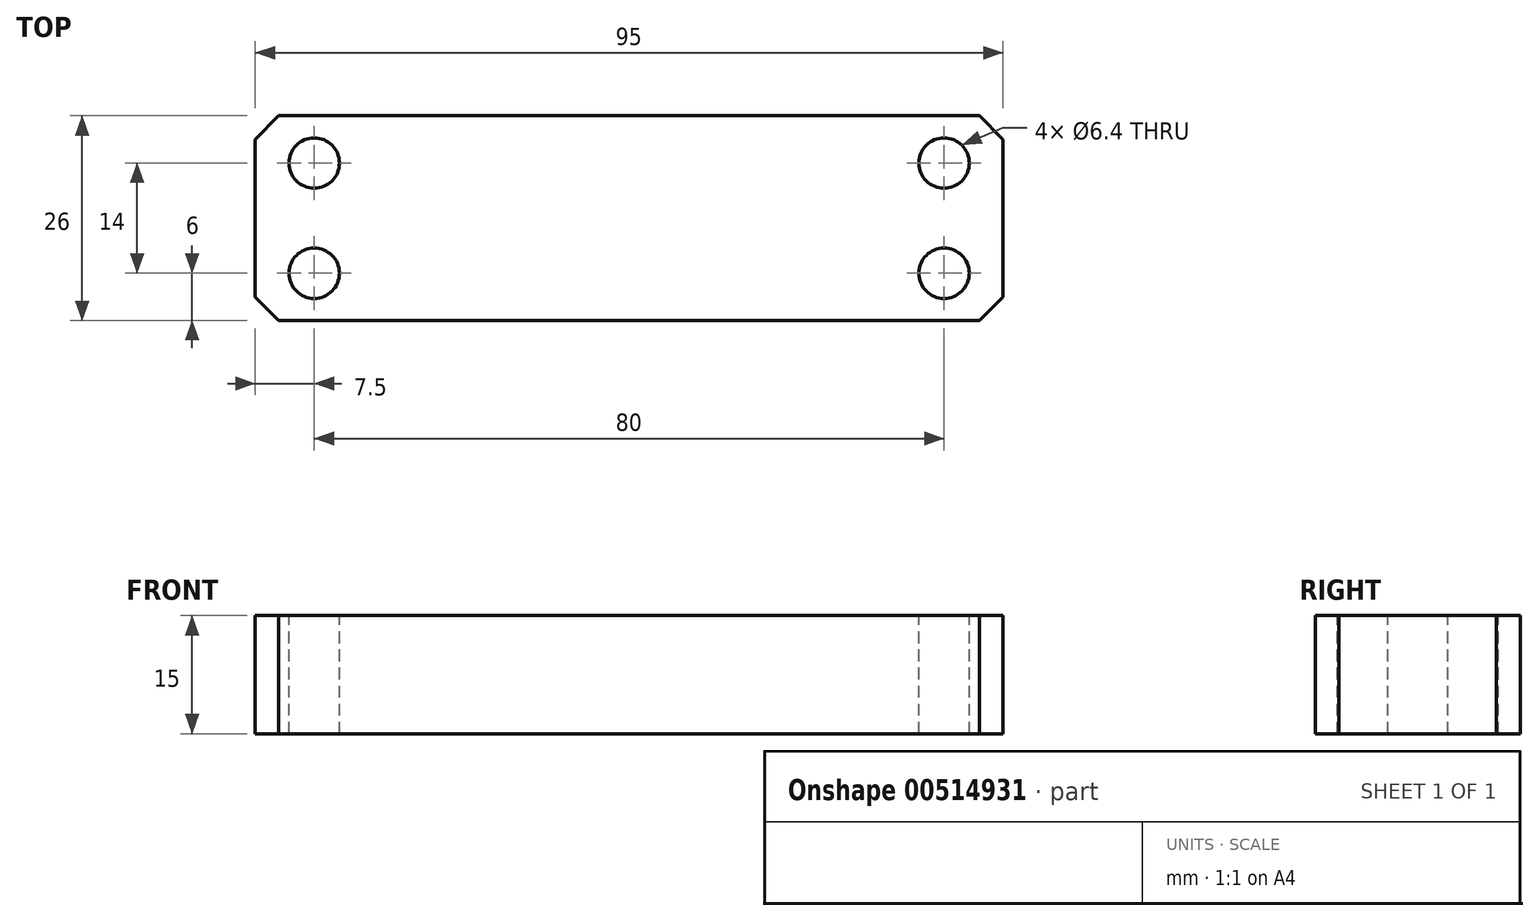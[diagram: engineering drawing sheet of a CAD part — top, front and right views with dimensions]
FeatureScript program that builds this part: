
annotation { "Feature Type Name" : "Feature", "Feature Type Description" : "" }
export const myFeature = defineFeature(function(context is Context, id is Id, definition is map)
    precondition{}
    {
        {
            var Q0;
            Q0=qCreatedBy(makeId("Top.planeOp"),FACE);
            var sketch = newSketch(context, id + "F0", { "sketchPlane" : qUnion([Q0])});
            skLineSegment(sketch, "E0.bottom", {"start": v(-47.5, 13) * mm, "end": v(47.5, 13) * mm});
            skLineSegment(sketch, "E0.top", {"start": v(-47.5, -13) * mm, "end": v(47.5, -13) * mm});
            skLineSegment(sketch, "E0.left", {"start": v(-47.5, 13) * mm, "end": v(-47.5, -13) * mm});
            skLineSegment(sketch, "E0.right", {"start": v(47.5, 13) * mm, "end": v(47.5, -13) * mm});
            skSolve(sketch);
        }
        {
            var Q0;
            Q0=makeQuery(id+"F0.imprint","IMPRINT",FACE,{"disambiguationData":[TD([[makeQuery(id+"F0.imprint","IMPRINT",EDGE,{"derivedFrom":sQuery(id+"F0.wireOp",EDGE,"E0.bottom")}),-1.0]])]});
            extrude(context, id + "F1", {"entities" : qUnion([Q0]), "endBound" : BoundingType.SYMMETRIC, "depth" : 15 * mm, "offsetDistance" : 25 * mm});
        }
        {
            var Q0;
            Q0=makeQuery(id+"F1.opExtrude","CAP_FACE",FACE,{"disambiguationData":[OSD([sQuery(id+"F0.wireOp",EDGE,"E0.bottom"),sQuery(id+"F0.wireOp",EDGE,"E0.top"),sQuery(id+"F0.wireOp",EDGE,"E0.left"),sQuery(id+"F0.wireOp",EDGE,"E0.right")])],"isStart":false});
            var sketch = newSketch(context, id + "F2", { "sketchPlane" : qUnion([Q0])});
            skPoint(sketch, "E1", {"position": v(-40, 7) * mm});
            skPoint(sketch, "E2", {"position": v(-40, -7) * mm});
            skPoint(sketch, "E3", {"position": v(40, -7) * mm});
            skPoint(sketch, "E4", {"position": v(40, 7) * mm});
            skSolve(sketch);
        }
        {
            var Q0;
            Q0=sQuery(id+"F2.wireOp",VERTEX,"E1");
            var Q1;
            Q1=sQuery(id+"F2.wireOp",VERTEX,"E2");
            var Q2;
            Q2=sQuery(id+"F2.wireOp",VERTEX,"E4");
            var Q3;
            Q3=sQuery(id+"F2.wireOp",VERTEX,"E3");
            var Q4;
            Q4=makeQuery(id+"F1.opExtrude","SWEPT_BODY",BODY,{"disambiguationData":[OSD([sQuery(id+"F0.wireOp",EDGE,"E0.bottom"),sQuery(id+"F0.wireOp",EDGE,"E0.top"),sQuery(id+"F0.wireOp",EDGE,"E0.left"),sQuery(id+"F0.wireOp",EDGE,"E0.right")])]});
            hole(context, id + "F3", {"style" : HoleStyle.SIMPLE, "endStyle" : HoleEndStyle.THROUGH, "holeDiameter" : 6.4 * mm, "isTappedThrough" : true, "tappedDepth" : 12 * mm, "tapClearance" : 3, "locations" : qUnion([Q0, Q1, Q2, Q3]), "scope" : qUnion([Q4])});
        }
        {
            var Q0;
            Q0=makeQuery(id+"F1.opExtrude","SWEPT_EDGE",EDGE,{"disambiguationData":[OSD([sQuery(id+"F0.wireOp",EDGE,"E0.bottom"),sQuery(id+"F0.wireOp",EDGE,"E0.left")])]});
            var Q1;
            Q1=makeQuery(id+"F1.opExtrude","SWEPT_EDGE",EDGE,{"disambiguationData":[OSD([sQuery(id+"F0.wireOp",EDGE,"E0.bottom"),sQuery(id+"F0.wireOp",EDGE,"E0.right")])]});
            var Q2;
            Q2=makeQuery(id+"F1.opExtrude","SWEPT_EDGE",EDGE,{"disambiguationData":[OSD([sQuery(id+"F0.wireOp",EDGE,"E0.top"),sQuery(id+"F0.wireOp",EDGE,"E0.right")])]});
            var Q3;
            Q3=makeQuery(id+"F1.opExtrude","SWEPT_EDGE",EDGE,{"disambiguationData":[OSD([sQuery(id+"F0.wireOp",EDGE,"E0.top"),sQuery(id+"F0.wireOp",EDGE,"E0.left")])]});
            chamfer(context, id + "F4", {"entities" : qUnion([Q0, Q1, Q2, Q3]), "width" : 3 * mm, "tangentPropagation" : true});
        }
    });
